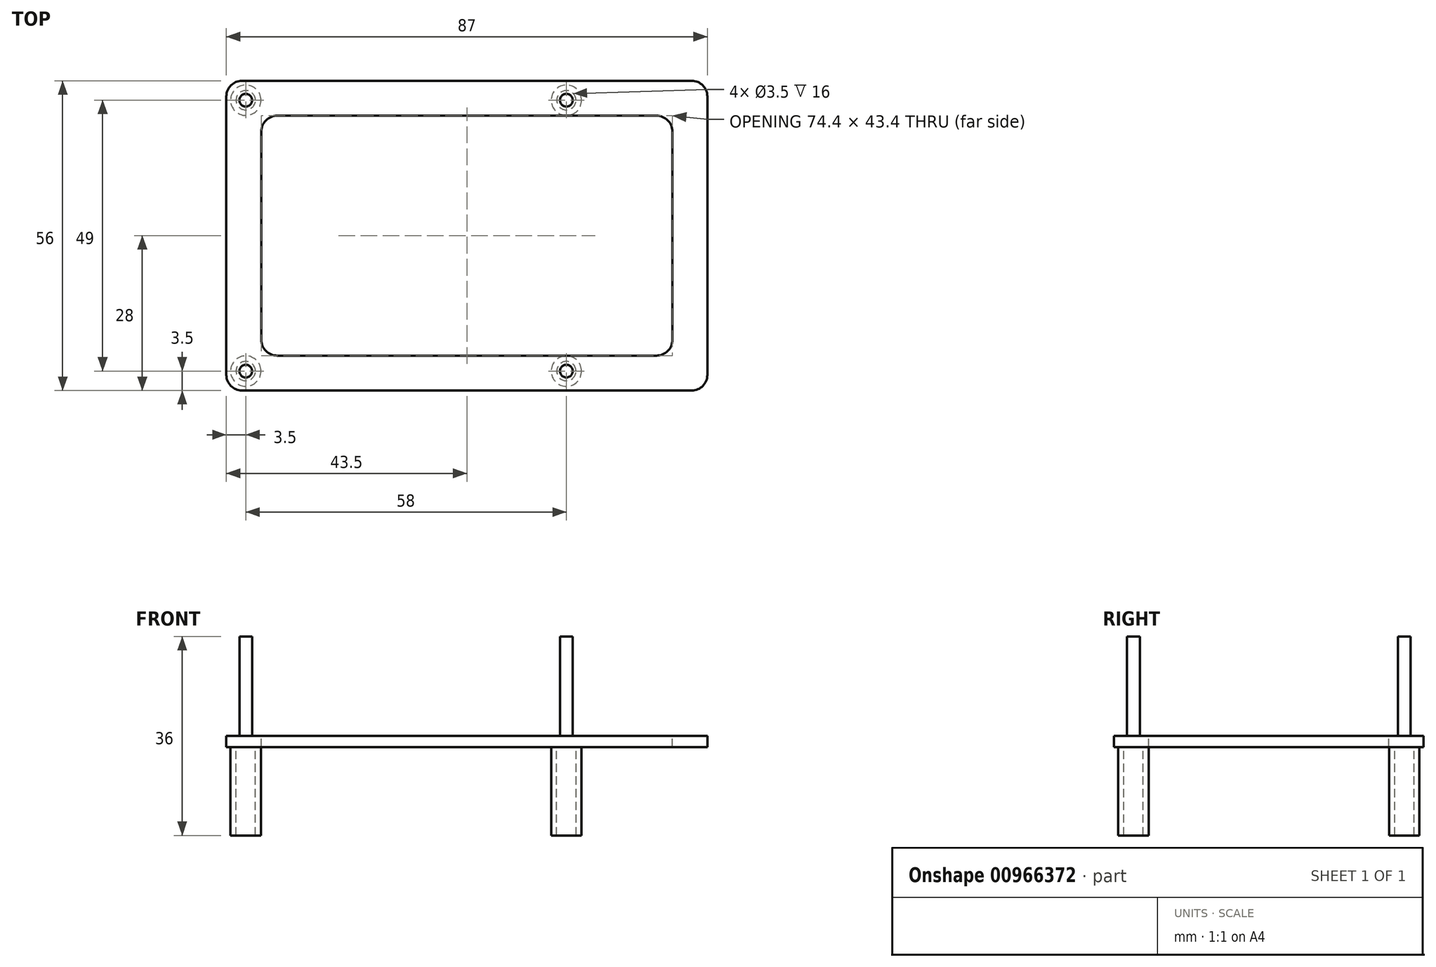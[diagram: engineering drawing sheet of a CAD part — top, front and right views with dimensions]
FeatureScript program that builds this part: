
annotation { "Feature Type Name" : "Feature", "Feature Type Description" : "" }
export const myFeature = defineFeature(function(context is Context, id is Id, definition is map)
    precondition{}
    {
        {
            var Q0;
            Q0=qCreatedBy(makeId("Top.planeOp"),FACE);
            var sketch = newSketch(context, id + "F0", { "sketchPlane" : qUnion([Q0])});
            skLineSegment(sketch, "E0.bottom", {"start": v(2.8, 0) * mm, "end": v(84.2, 0) * mm});
            skLineSegment(sketch, "E0.top", {"start": v(2.8, 56) * mm, "end": v(84.2, 56) * mm});
            skLineSegment(sketch, "E0.left", {"start": v(0, 2.8) * mm, "end": v(0, 53.2) * mm});
            skLineSegment(sketch, "E0.right", {"start": v(87, 2.8) * mm, "end": v(87, 53.2) * mm});
            skCircle(sketch, "E1", {"center": v(3.5, 3.5) * mm, "radius": 1.15 * mm});
            skCircle(sketch, "E2", {"center": v(3.5, 52.5) * mm, "radius": 1.15 * mm});
            skCircle(sketch, "E3", {"center": v(61.5, 52.5) * mm, "radius": 1.15 * mm});
            skCircle(sketch, "E4", {"center": v(61.5, 3.5) * mm, "radius": 1.15 * mm});
            skPoint(sketch, "E5.visualSharp", {"position": v(0, 0) * mm});
            skArc(sketch, "E5.filletArc", {"start": v(0, 2.8) * mm, "mid": v(0.82, 0.82) * mm, "end": v(2.8, 0) * mm});
            skPoint(sketch, "E6.visualSharp", {"position": v(87, 0) * mm});
            skArc(sketch, "E6.filletArc", {"start": v(84.2, 0) * mm, "mid": v(86.18, 0.82) * mm, "end": v(87, 2.8) * mm});
            skPoint(sketch, "E7.visualSharp", {"position": v(87, 56) * mm});
            skArc(sketch, "E7.filletArc", {"start": v(87, 53.2) * mm, "mid": v(86.18, 55.18) * mm, "end": v(84.2, 56) * mm});
            skPoint(sketch, "E8.visualSharp", {"position": v(0, 56) * mm});
            skArc(sketch, "E8.filletArc", {"start": v(2.8, 56) * mm, "mid": v(0.82, 55.18) * mm, "end": v(0, 53.2) * mm});
            skSolve(sketch);
        }
        {
            var Q0;
            Q0=makeQuery(id+"F0.imprint","IMPRINT",FACE,{"disambiguationData":[TD([[makeQuery(id+"F0.imprint","IMPRINT",EDGE,{"derivedFrom":sQuery(id+"F0.wireOp",EDGE,"E0.bottom")}),1.0]])]});
            var Q1;
            Q1=makeQuery(id+"F0.imprint","IMPRINT",FACE,{"disambiguationData":[TD([[makeQuery(id+"F0.imprint","IMPRINT",EDGE,{"derivedFrom":sQuery(id+"F0.wireOp",EDGE,"E1")}),1.0]])]});
            var Q2;
            Q2=makeQuery(id+"F0.imprint","IMPRINT",FACE,{"disambiguationData":[TD([[makeQuery(id+"F0.imprint","IMPRINT",EDGE,{"derivedFrom":sQuery(id+"F0.wireOp",EDGE,"E3")}),1.0]])]});
            var Q3;
            Q3=makeQuery(id+"F0.imprint","IMPRINT",FACE,{"disambiguationData":[TD([[makeQuery(id+"F0.imprint","IMPRINT",EDGE,{"derivedFrom":sQuery(id+"F0.wireOp",EDGE,"E4")}),1.0]])]});
            var Q4;
            Q4=makeQuery(id+"F0.imprint","IMPRINT",FACE,{"disambiguationData":[TD([[makeQuery(id+"F0.imprint","IMPRINT",EDGE,{"derivedFrom":sQuery(id+"F0.wireOp",EDGE,"E3")}),1.0]])]});
            var Q5;
            Q5=makeQuery(id+"F0.imprint","IMPRINT",FACE,{"disambiguationData":[TD([[makeQuery(id+"F0.imprint","IMPRINT",EDGE,{"derivedFrom":sQuery(id+"F0.wireOp",EDGE,"E4")}),1.0]])]});
            var Q6;
            Q6=makeQuery(id+"F0.imprint","IMPRINT",FACE,{"disambiguationData":[TD([[makeQuery(id+"F0.imprint","IMPRINT",EDGE,{"derivedFrom":sQuery(id+"F0.wireOp",EDGE,"E2")}),1.0]])]});
            extrude(context, id + "F1", {"entities" : qUnion([Q0, Q1, Q2, Q3, Q4, Q5, Q6]), "depth" : 2 * mm, "offsetDistance" : 25 * mm});
        }
        {
            var Q0;
            Q0=makeQuery(id+"F0.imprint","IMPRINT",FACE,{"disambiguationData":[TD([[makeQuery(id+"F0.imprint","IMPRINT",EDGE,{"derivedFrom":sQuery(id+"F0.wireOp",EDGE,"E4")}),1.0]])]});
            var Q1;
            Q1=makeQuery(id+"F0.imprint","IMPRINT",FACE,{"disambiguationData":[TD([[makeQuery(id+"F0.imprint","IMPRINT",EDGE,{"derivedFrom":sQuery(id+"F0.wireOp",EDGE,"E3")}),1.0]])]});
            var Q2;
            Q2=makeQuery(id+"F0.imprint","IMPRINT",FACE,{"disambiguationData":[TD([[makeQuery(id+"F0.imprint","IMPRINT",EDGE,{"derivedFrom":sQuery(id+"F0.wireOp",EDGE,"E2")}),1.0]])]});
            var Q3;
            Q3=makeQuery(id+"F0.imprint","IMPRINT",FACE,{"disambiguationData":[TD([[makeQuery(id+"F0.imprint","IMPRINT",EDGE,{"derivedFrom":sQuery(id+"F0.wireOp",EDGE,"E1")}),1.0]])]});
            extrude(context, id + "F2", {"entities" : qUnion([Q0, Q1, Q2, Q3]), "operationType" : NewBodyOperationType.ADD, "depth" : 105 * mm, "offsetDistance" : 25 * mm});
        }
        {
            var Q0;
            Q0=qCreatedBy(makeId("Top.planeOp"),FACE);
            cPlane(context, id + "F3", {"entities" : qUnion([Q0]), "cplaneType" : CPlaneType.OFFSET, "offset" : 25 * mm, "width" : 150 * mm, "height" : 150 * mm});
        }
        {
            var Q0;
            Q0=qCreatedBy(id+"F3.planeOp",FACE);
            var sketch = newSketch(context, id + "F4", { "sketchPlane" : qUnion([Q0])});
            skPoint(sketch, "E9.0", {"position": v(3.5, 52.5) * mm});
            skPoint(sketch, "E10.0", {"position": v(61.5, 52.5) * mm});
            skPoint(sketch, "E11.0", {"position": v(3.5, 3.5) * mm});
            skPoint(sketch, "E12.0", {"position": v(61.5, 3.5) * mm});
            skLineSegment(sketch, "E13.0", {"start": v(2.8, 56) * mm, "end": v(84.2, 56) * mm});
            skPoint(sketch, "E14.0", {"position": v(0.82, 55.18) * mm});
            skLineSegment(sketch, "E15.0", {"start": v(0, 2.8) * mm, "end": v(0, 53.2) * mm});
            skArc(sketch, "E16.0", {"start": v(2.8, 56) * mm, "mid": v(0.82, 55.18) * mm, "end": v(0, 53.2) * mm});
            skArc(sketch, "E17.0", {"start": v(87, 53.2) * mm, "mid": v(86.18, 55.18) * mm, "end": v(84.2, 56) * mm});
            skLineSegment(sketch, "E18.0", {"start": v(87, 2.8) * mm, "end": v(87, 53.2) * mm});
            skLineSegment(sketch, "E19.0", {"start": v(2.8, 0) * mm, "end": v(84.2, 0) * mm});
            skArc(sketch, "E20.0", {"start": v(84.2, 0) * mm, "mid": v(86.18, 0.82) * mm, "end": v(87, 2.8) * mm});
            skArc(sketch, "E21.0", {"start": v(0, 2.8) * mm, "mid": v(0.82, 0.82) * mm, "end": v(2.8, 0) * mm});
            skCircle(sketch, "E22", {"center": v(3.5, 52.5) * mm, "radius": 1.75 * mm});
            skCircle(sketch, "E23", {"center": v(3.5, 3.5) * mm, "radius": 1.75 * mm});
            skCircle(sketch, "E24", {"center": v(61.5, 3.5) * mm, "radius": 1.75 * mm});
            skCircle(sketch, "E25", {"center": v(61.5, 52.5) * mm, "radius": 1.75 * mm});
            skCircle(sketch, "E26", {"center": v(3.5, 3.5) * mm, "radius": 2.75 * mm});
            skCircle(sketch, "E27", {"center": v(61.5, 3.5) * mm, "radius": 2.75 * mm});
            skCircle(sketch, "E28", {"center": v(3.5, 52.5) * mm, "radius": 2.75 * mm});
            skCircle(sketch, "E29", {"center": v(61.5, 52.5) * mm, "radius": 2.75 * mm});
            skSolve(sketch);
        }
        {
            var Q0;
            Q0=makeQuery(id+"F4.imprint","IMPRINT",FACE,{"disambiguationData":[TD([[makeQuery(id+"F4.imprint","IMPRINT",EDGE,{"derivedFrom":sQuery(id+"F4.wireOp",EDGE,"E23")}),1.0]])]});
            var Q1;
            Q1=makeQuery(id+"F4.imprint","IMPRINT",FACE,{"disambiguationData":[TD([[makeQuery(id+"F4.imprint","IMPRINT",EDGE,{"derivedFrom":sQuery(id+"F4.wireOp",EDGE,"E23")}),-1.0]])]});
            var Q2;
            Q2=makeQuery(id+"F4.imprint","IMPRINT",FACE,{"disambiguationData":[TD([[makeQuery(id+"F4.imprint","IMPRINT",EDGE,{"derivedFrom":sQuery(id+"F4.wireOp",EDGE,"E13.0")}),-1.0]])]});
            var Q3;
            Q3=makeQuery(id+"F4.imprint","IMPRINT",FACE,{"disambiguationData":[TD([[makeQuery(id+"F4.imprint","IMPRINT",EDGE,{"derivedFrom":sQuery(id+"F4.wireOp",EDGE,"E24")}),-1.0]])]});
            var Q4;
            Q4=makeQuery(id+"F4.imprint","IMPRINT",FACE,{"disambiguationData":[TD([[makeQuery(id+"F4.imprint","IMPRINT",EDGE,{"derivedFrom":sQuery(id+"F4.wireOp",EDGE,"E24")}),1.0]])]});
            var Q5;
            Q5=makeQuery(id+"F4.imprint","IMPRINT",FACE,{"disambiguationData":[TD([[makeQuery(id+"F4.imprint","IMPRINT",EDGE,{"derivedFrom":sQuery(id+"F4.wireOp",EDGE,"E25")}),-1.0]])]});
            var Q6;
            Q6=makeQuery(id+"F4.imprint","IMPRINT",FACE,{"disambiguationData":[TD([[makeQuery(id+"F4.imprint","IMPRINT",EDGE,{"derivedFrom":sQuery(id+"F4.wireOp",EDGE,"E25")}),1.0]])]});
            var Q7;
            Q7=makeQuery(id+"F4.imprint","IMPRINT",FACE,{"disambiguationData":[TD([[makeQuery(id+"F4.imprint","IMPRINT",EDGE,{"derivedFrom":sQuery(id+"F4.wireOp",EDGE,"E22")}),-1.0]])]});
            var Q8;
            Q8=makeQuery(id+"F4.imprint","IMPRINT",FACE,{"disambiguationData":[TD([[makeQuery(id+"F4.imprint","IMPRINT",EDGE,{"derivedFrom":sQuery(id+"F4.wireOp",EDGE,"E22")}),1.0]])]});
            extrude(context, id + "F5", {"entities" : qUnion([Q0, Q1, Q2, Q3, Q4, Q5, Q6, Q7, Q8]), "depth" : 2 * mm, "offsetDistance" : 25 * mm});
        }
        {
            var Q0;
            Q0=makeQuery(id+"F4.imprint","IMPRINT",FACE,{"disambiguationData":[TD([[makeQuery(id+"F4.imprint","IMPRINT",EDGE,{"derivedFrom":sQuery(id+"F4.wireOp",EDGE,"E23")}),-1.0]])]});
            var Q1;
            Q1=makeQuery(id+"F4.imprint","IMPRINT",FACE,{"disambiguationData":[TD([[makeQuery(id+"F4.imprint","IMPRINT",EDGE,{"derivedFrom":sQuery(id+"F4.wireOp",EDGE,"E22")}),-1.0]])]});
            var Q2;
            Q2=makeQuery(id+"F4.imprint","IMPRINT",FACE,{"disambiguationData":[TD([[makeQuery(id+"F4.imprint","IMPRINT",EDGE,{"derivedFrom":sQuery(id+"F4.wireOp",EDGE,"E25")}),-1.0]])]});
            var Q3;
            Q3=makeQuery(id+"F4.imprint","IMPRINT",FACE,{"disambiguationData":[TD([[makeQuery(id+"F4.imprint","IMPRINT",EDGE,{"derivedFrom":sQuery(id+"F4.wireOp",EDGE,"E24")}),-1.0]])]});
            var Q4;
            Q4=makeQuery(id+"F5.opExtrude","CAP_FACE",FACE,{"disambiguationData":[OSD([sQuery(id+"F4.wireOp",EDGE,"E13.0"),sQuery(id+"F4.wireOp",EDGE,"E15.0"),sQuery(id+"F4.wireOp",EDGE,"E16.0"),sQuery(id+"F4.wireOp",EDGE,"E17.0"),sQuery(id+"F4.wireOp",EDGE,"E18.0"),sQuery(id+"F4.wireOp",EDGE,"E19.0"),sQuery(id+"F4.wireOp",EDGE,"E20.0"),sQuery(id+"F4.wireOp",EDGE,"E21.0"),sQuery(id+"F4.wireOp",EDGE,"E26"),sQuery(id+"F4.wireOp",EDGE,"E27"),sQuery(id+"F4.wireOp",EDGE,"E28"),sQuery(id+"F4.wireOp",EDGE,"E29")])],"isStart":false});
            var Q5;
            Q5=makeQuery(id+"F5.opExtrude","SWEPT_BODY",BODY,{"disambiguationData":[OSD([sQuery(id+"F4.wireOp",EDGE,"E13.0"),sQuery(id+"F4.wireOp",EDGE,"E15.0"),sQuery(id+"F4.wireOp",EDGE,"E16.0"),sQuery(id+"F4.wireOp",EDGE,"E17.0"),sQuery(id+"F4.wireOp",EDGE,"E18.0"),sQuery(id+"F4.wireOp",EDGE,"E19.0"),sQuery(id+"F4.wireOp",EDGE,"E20.0"),sQuery(id+"F4.wireOp",EDGE,"E21.0"),sQuery(id+"F4.wireOp",EDGE,"E26"),sQuery(id+"F4.wireOp",EDGE,"E27"),sQuery(id+"F4.wireOp",EDGE,"E28"),sQuery(id+"F4.wireOp",EDGE,"E29")])]});
            extrude(context, id + "F6", {"entities" : qUnion([Q0, Q1, Q2, Q3]), "operationType" : NewBodyOperationType.ADD, "endBound" : BoundingType.UP_TO_SURFACE, "depth" : 20 * mm, "endBoundEntityFace" : qUnion([Q4]), "endBoundEntityBody" : qUnion([Q5]), "offsetDistance" : 25 * mm});
        }
        {
            var Q0;
            Q0=makeQuery(id+"F4.imprint","IMPRINT",FACE,{"disambiguationData":[TD([[makeQuery(id+"F4.imprint","IMPRINT",EDGE,{"derivedFrom":sQuery(id+"F4.wireOp",EDGE,"E23")}),-1.0]])]});
            var Q1;
            Q1=makeQuery(id+"F4.imprint","IMPRINT",FACE,{"disambiguationData":[TD([[makeQuery(id+"F4.imprint","IMPRINT",EDGE,{"derivedFrom":sQuery(id+"F4.wireOp",EDGE,"E22")}),-1.0]])]});
            var Q2;
            Q2=makeQuery(id+"F4.imprint","IMPRINT",FACE,{"disambiguationData":[TD([[makeQuery(id+"F4.imprint","IMPRINT",EDGE,{"derivedFrom":sQuery(id+"F4.wireOp",EDGE,"E24")}),-1.0]])]});
            var Q3;
            Q3=makeQuery(id+"F4.imprint","IMPRINT",FACE,{"disambiguationData":[TD([[makeQuery(id+"F4.imprint","IMPRINT",EDGE,{"derivedFrom":sQuery(id+"F4.wireOp",EDGE,"E25")}),-1.0]])]});
            extrude(context, id + "F7", {"entities" : qUnion([Q0, Q1, Q2, Q3]), "operationType" : NewBodyOperationType.ADD, "oppositeDirection" : true, "depth" : 16 * mm, "offsetDistance" : 25 * mm});
        }
        {
            var Q0;
            Q0=makeQuery(id+"F1.opExtrude","SWEPT_BODY",BODY,{"disambiguationData":[OSD([sQuery(id+"F0.wireOp",EDGE,"E0.bottom"),sQuery(id+"F0.wireOp",EDGE,"E0.top"),sQuery(id+"F0.wireOp",EDGE,"E0.left"),sQuery(id+"F0.wireOp",EDGE,"E0.right"),sQuery(id+"F0.wireOp",EDGE,"E5.filletArc"),sQuery(id+"F0.wireOp",EDGE,"E6.filletArc"),sQuery(id+"F0.wireOp",EDGE,"E7.filletArc"),sQuery(id+"F0.wireOp",EDGE,"E8.filletArc")])]});
            deleteBodies(context, id + "F8", {"entities" : qUnion([Q0])});
        }
        {
            var Q0;
            Q0=makeQuery(id+"F5.opExtrude","CAP_FACE",FACE,{"disambiguationData":[OSD([sQuery(id+"F4.wireOp",EDGE,"E13.0"),sQuery(id+"F4.wireOp",EDGE,"E15.0"),sQuery(id+"F4.wireOp",EDGE,"E16.0"),sQuery(id+"F4.wireOp",EDGE,"E17.0"),sQuery(id+"F4.wireOp",EDGE,"E18.0"),sQuery(id+"F4.wireOp",EDGE,"E19.0"),sQuery(id+"F4.wireOp",EDGE,"E20.0"),sQuery(id+"F4.wireOp",EDGE,"E21.0")])],"isStart":false});
            var sketch = newSketch(context, id + "F9", { "sketchPlane" : qUnion([Q0])});
            skCircle(sketch, "E30.0", {"center": v(3.5, 52.5) * mm, "radius": 1.15 * mm});
            skCircle(sketch, "E31.0", {"center": v(61.5, 52.5) * mm, "radius": 1.15 * mm});
            skCircle(sketch, "E32.0", {"center": v(61.5, 3.5) * mm, "radius": 1.15 * mm});
            skCircle(sketch, "E33.0", {"center": v(3.5, 3.5) * mm, "radius": 1.15 * mm});
            skSolve(sketch);
        }
        {
            var Q0;
            Q0 = qSketchRegion(id + "F9", true);
            extrude(context, id + "F10", {"entities" : qUnion([Q0]), "operationType" : NewBodyOperationType.ADD, "depth" : 18 * mm, "offsetDistance" : 25 * mm});
        }
        {
            var Q0;
            Q0=makeQuery(id+"F5.opExtrude","CAP_FACE",FACE,{"disambiguationData":[OSD([sQuery(id+"F4.wireOp",EDGE,"E13.0"),sQuery(id+"F4.wireOp",EDGE,"E15.0"),sQuery(id+"F4.wireOp",EDGE,"E16.0"),sQuery(id+"F4.wireOp",EDGE,"E17.0"),sQuery(id+"F4.wireOp",EDGE,"E18.0"),sQuery(id+"F4.wireOp",EDGE,"E19.0"),sQuery(id+"F4.wireOp",EDGE,"E20.0"),sQuery(id+"F4.wireOp",EDGE,"E21.0")])],"isStart":false});
            var sketch = newSketch(context, id + "F11", { "sketchPlane" : qUnion([Q0])});
            skLineSegment(sketch, "E34.0", {"start": v(2.8, 56) * mm, "end": v(84.2, 56) * mm});
            skPoint(sketch, "E35.0", {"position": v(2.8, 56) * mm});
            skPoint(sketch, "E36.0", {"position": v(0.82, 55.18) * mm});
            skPoint(sketch, "E37.0", {"position": v(0, 53.2) * mm});
            skArc(sketch, "E38.0", {"start": v(2.8, 56) * mm, "mid": v(0.82, 55.18) * mm, "end": v(0, 53.2) * mm});
            skLineSegment(sketch, "E39.0", {"start": v(0, 2.8) * mm, "end": v(0, 53.2) * mm});
            skArc(sketch, "E40.0", {"start": v(0, 2.8) * mm, "mid": v(0.82, 0.82) * mm, "end": v(2.8, 0) * mm});
            skLineSegment(sketch, "E41.0", {"start": v(2.8, 0) * mm, "end": v(84.2, 0) * mm});
            skPoint(sketch, "E42.0", {"position": v(0, 2.8) * mm});
            skArc(sketch, "E43.0", {"start": v(84.2, 0) * mm, "mid": v(86.18, 0.82) * mm, "end": v(87, 2.8) * mm});
            skLineSegment(sketch, "E44.0", {"start": v(87, 2.8) * mm, "end": v(87, 53.2) * mm});
            skLineSegment(sketch, "E45.1", {"start": v(6.3, 9.2) * mm, "end": v(6.3, 46.8) * mm});
            skLineSegment(sketch, "E45.2", {"start": v(9.2, 6.3) * mm, "end": v(77.8, 6.3) * mm});
            skLineSegment(sketch, "E45.5", {"start": v(80.7, 9.2) * mm, "end": v(80.7, 46.8) * mm});
            skLineSegment(sketch, "E45.7", {"start": v(9.2, 49.7) * mm, "end": v(77.8, 49.7) * mm});
            skPoint(sketch, "E46.visualSharp", {"position": v(6.3, 49.7) * mm});
            skArc(sketch, "E46.filletArc", {"start": v(9.2, 49.7) * mm, "mid": v(7.15, 48.85) * mm, "end": v(6.3, 46.8) * mm});
            skPoint(sketch, "E47.visualSharp", {"position": v(6.3, 6.3) * mm});
            skArc(sketch, "E47.filletArc", {"start": v(6.3, 9.2) * mm, "mid": v(7.15, 7.15) * mm, "end": v(9.2, 6.3) * mm});
            skPoint(sketch, "E48.visualSharp", {"position": v(80.7, 6.3) * mm});
            skArc(sketch, "E48.filletArc", {"start": v(77.8, 6.3) * mm, "mid": v(79.85, 7.15) * mm, "end": v(80.7, 9.2) * mm});
            skPoint(sketch, "E49.visualSharp", {"position": v(80.7, 49.7) * mm});
            skArc(sketch, "E49.filletArc", {"start": v(80.7, 46.8) * mm, "mid": v(79.85, 48.85) * mm, "end": v(77.8, 49.7) * mm});
            skSolve(sketch);
        }
        {
            var Q0;
            Q0=makeQuery(id+"F11.imprint","IMPRINT",FACE,{"disambiguationData":[TD([[makeQuery(id+"F11.imprint","IMPRINT",EDGE,{"derivedFrom":sQuery(id+"F11.wireOp",EDGE,"E45.1")}),-1.0]])]});
            extrude(context, id + "F12", {"entities" : qUnion([Q0]), "operationType" : NewBodyOperationType.REMOVE, "oppositeDirection" : true, "depth" : 2 * mm, "offsetDistance" : 25 * mm});
        }
    });
